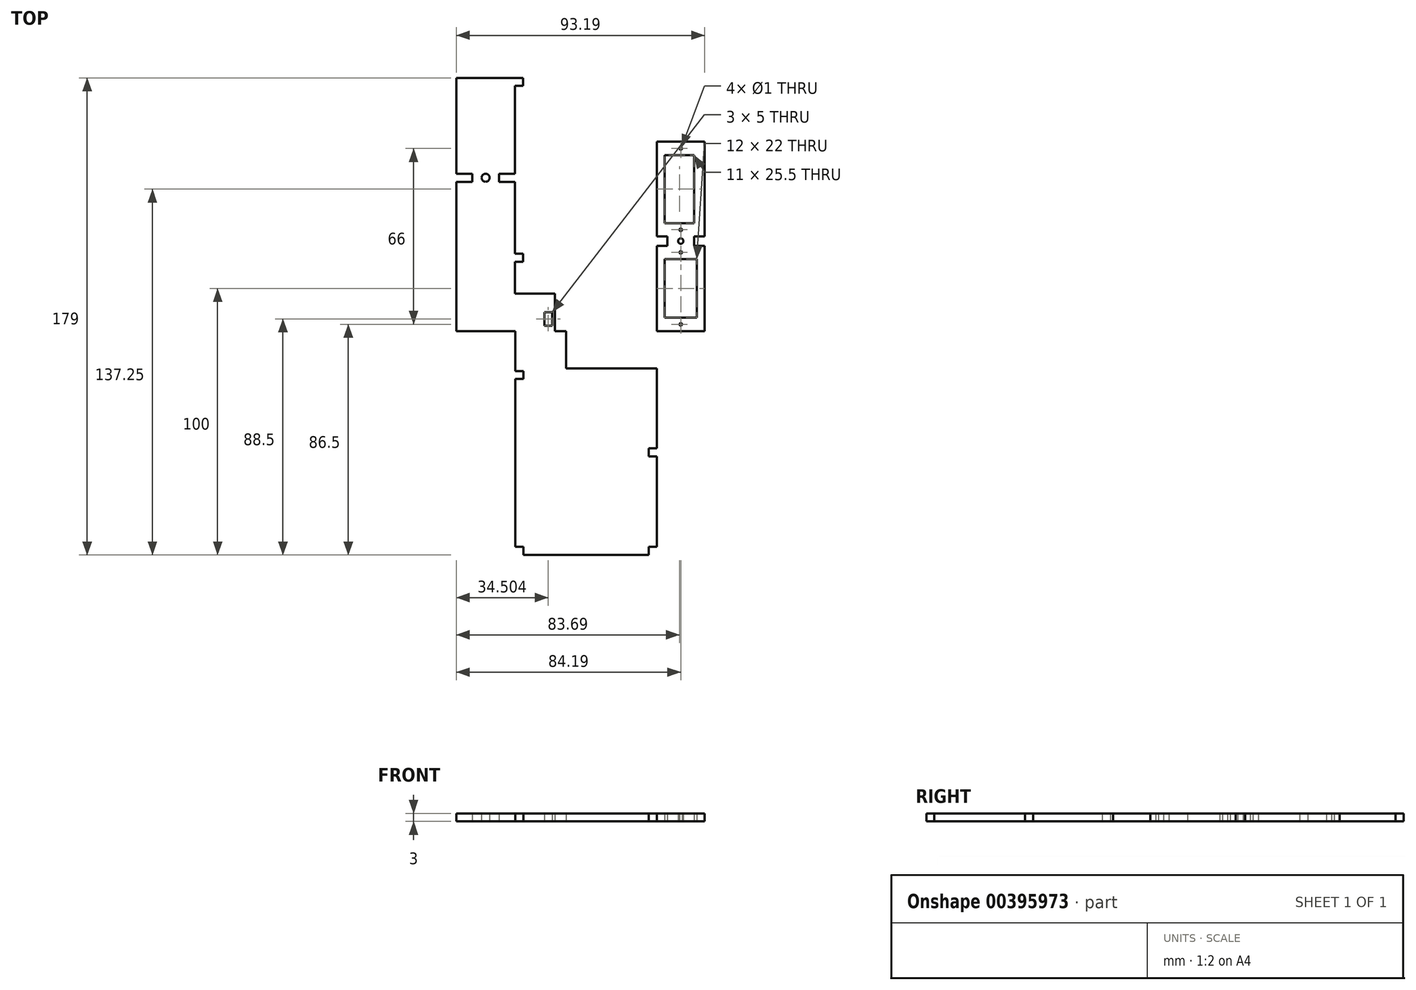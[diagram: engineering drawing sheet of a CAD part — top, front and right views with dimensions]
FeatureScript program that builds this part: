
annotation { "Feature Type Name" : "Feature", "Feature Type Description" : "" }
export const myFeature = defineFeature(function(context is Context, id is Id, definition is map)
    precondition{}
    {
        {
            var Q0;
            Q0=qCreatedBy(makeId("Top.planeOp"),FACE);
            var sketch = newSketch(context, id + "F0", { "sketchPlane" : qUnion([Q0])});
            skLineSegment(sketch, "E0", {"start": v(0, 0) * mm, "end": v(0, 32) * mm});
            skLineSegment(sketch, "E1", {"start": v(0, 71) * mm, "end": v(18, 71) * mm});
            skLineSegment(sketch, "E2", {"start": v(18, 71) * mm, "end": v(18, 35.5) * mm});
            skLineSegment(sketch, "E3", {"start": v(18, 0) * mm, "end": v(0, 0) * mm});
            skLineSegment(sketch, "E4", {"start": v(18, 71) * mm, "end": v(18, 38) * mm});
            skLineSegment(sketch, "E5", {"start": v(9, 5) * mm, "end": v(18, 5) * mm});
            skLineSegment(sketch, "E6", {"start": v(18, 5) * mm, "end": v(0, 5) * mm});
            skLineSegment(sketch, "E7", {"start": v(2.25, 5) * mm, "end": v(9, 5) * mm});
            skLineSegment(sketch, "E8", {"start": v(3, 5) * mm, "end": v(4.5, 5) * mm});
            skLineSegment(sketch, "E9", {"start": v(0, 5) * mm, "end": v(0, 32) * mm});
            skLineSegment(sketch, "E10", {"start": v(0, 5) * mm, "end": v(0, 27) * mm});
            skLineSegment(sketch, "E11", {"start": v(0, 27) * mm, "end": v(18, 27) * mm});
            skLineSegment(sketch, "E12", {"start": v(0, 5) * mm, "end": v(2.25, 5) * mm});
            skLineSegment(sketch, "E13", {"start": v(0, 5) * mm, "end": v(3, 5) * mm});
            skLineSegment(sketch, "E14", {"start": v(3, 5) * mm, "end": v(3, 27) * mm});
            skLineSegment(sketch, "E15", {"start": v(18, 5) * mm, "end": v(13.5, 5) * mm});
            skLineSegment(sketch, "E16", {"start": v(18, 5) * mm, "end": v(15, 5) * mm});
            skLineSegment(sketch, "E17", {"start": v(15, 5) * mm, "end": v(15, 27) * mm});
            skLineSegment(sketch, "E18", {"start": v(0, 27) * mm, "end": v(0, 32) * mm});
            skLineSegment(sketch, "E19", {"start": v(0, 32) * mm, "end": v(18, 32) * mm});
            skLineSegment(sketch, "E20", {"start": v(0, 32) * mm, "end": v(4, 32) * mm});
            skLineSegment(sketch, "E21", {"start": v(4, 32) * mm, "end": v(4, 35.5) * mm});
            skLineSegment(sketch, "E22", {"start": v(4, 35.5) * mm, "end": v(18, 35.5) * mm});
            skLineSegment(sketch, "E23", {"start": v(18, 32) * mm, "end": v(14, 32) * mm});
            skLineSegment(sketch, "E24", {"start": v(14, 32) * mm, "end": v(14, 35.5) * mm});
            skLineSegment(sketch, "E25", {"start": v(4, 35.5) * mm, "end": v(0, 35.5) * mm});
            skLineSegment(sketch, "E26", {"start": v(4, 35.5) * mm, "end": v(4, 40.5) * mm});
            skLineSegment(sketch, "E27", {"start": v(4, 40.5) * mm, "end": v(18, 40.5) * mm});
            skLineSegment(sketch, "E28", {"start": v(18, 40.5) * mm, "end": v(0, 40.5) * mm});
            skLineSegment(sketch, "E29", {"start": v(0, 40.5) * mm, "end": v(3, 40.5) * mm});
            skLineSegment(sketch, "E30", {"start": v(3, 40.5) * mm, "end": v(3, 71) * mm});
            skLineSegment(sketch, "E31", {"start": v(3, 71) * mm, "end": v(14, 71) * mm});
            skLineSegment(sketch, "E32", {"start": v(14, 71) * mm, "end": v(14, 40.5) * mm});
            skLineSegment(sketch, "E33", {"start": v(0, 32) * mm, "end": v(0, 0) * mm});
            skLineSegment(sketch, "E34", {"start": v(18, 0) * mm, "end": v(18, 27) * mm});
            skLineSegment(sketch, "E35", {"start": v(18, 27) * mm, "end": v(18, 32) * mm});
            skLineSegment(sketch, "E36", {"start": v(18, 71) * mm, "end": v(18, 40.5) * mm});
            skLineSegment(sketch, "E37", {"start": v(0, 71) * mm, "end": v(0, 66) * mm});
            skLineSegment(sketch, "E38", {"start": v(0, 66) * mm, "end": v(18, 66) * mm});
            skLineSegment(sketch, "E39", {"start": v(0, 66) * mm, "end": v(0, 40.5) * mm});
            skLineSegment(sketch, "E40", {"start": v(0, 35.5) * mm, "end": v(0, 71) * mm});
            skLineSegment(sketch, "E41.trimOffspring", {"start": v(18, 32) * mm, "end": v(18, 0) * mm});
            skPoint(sketch, "E42.end.orphan", {"position": v(3, 0) * mm});
            skLineSegment(sketch, "E43", {"start": v(3, 5) * mm, "end": v(2.25, 5) * mm});
            skLineSegment(sketch, "E44", {"start": v(0, 5) * mm, "end": v(18, 5) * mm});
            skLineSegment(sketch, "E45", {"start": v(4, 35.5) * mm, "end": v(4, 33.75) * mm});
            skLineSegment(sketch, "E46", {"start": v(4, 33.75) * mm, "end": v(14, 33.75) * mm});
            skLineSegment(sketch, "E47", {"start": v(14, 35.5) * mm, "end": v(9, 35.5) * mm});
            skLineSegment(sketch, "E48", {"start": v(9, 35.5) * mm, "end": v(9, 32) * mm});
            skCircle(sketch, "E49", {"center": v(9, 33.75) * mm, "radius": 1 * mm});
            skLineSegment(sketch, "E50", {"start": v(3, 71) * mm, "end": v(3, 68.5) * mm});
            skLineSegment(sketch, "E51", {"start": v(3, 68.5) * mm, "end": v(14, 68.5) * mm});
            skLineSegment(sketch, "E52", {"start": v(14, 68.5) * mm, "end": v(14, 71) * mm});
            skLineSegment(sketch, "E53", {"start": v(9, 71) * mm, "end": v(9, 66) * mm});
            skCircle(sketch, "E54", {"center": v(9, 68.5) * mm, "radius": 0.5 * mm});
            skLineSegment(sketch, "E55", {"start": v(0, 5) * mm, "end": v(8, 5) * mm});
            skLineSegment(sketch, "E56", {"start": v(0, 0) * mm, "end": v(0, 2.5) * mm});
            skLineSegment(sketch, "E57", {"start": v(0, 2.5) * mm, "end": v(18, 2.5) * mm});
            skLineSegment(sketch, "E58", {"start": v(0, 0) * mm, "end": v(9, 0) * mm});
            skLineSegment(sketch, "E59", {"start": v(9, 0) * mm, "end": v(9, 5) * mm});
            skCircle(sketch, "E60", {"center": v(9, 2.5) * mm, "radius": 0.5 * mm});
            skLineSegment(sketch, "E61", {"start": v(0, 29.5) * mm, "end": v(18, 29.5) * mm});
            skLineSegment(sketch, "E62", {"start": v(9, 27) * mm, "end": v(9, 32) * mm});
            skCircle(sketch, "E63", {"center": v(9, 29.5) * mm, "radius": 0.5 * mm});
            skLineSegment(sketch, "E64", {"start": v(9, 32) * mm, "end": v(9, 40.5) * mm});
            skLineSegment(sketch, "E65", {"start": v(0, 40.5) * mm, "end": v(0, 38) * mm});
            skLineSegment(sketch, "E66", {"start": v(0, 38) * mm, "end": v(18, 38) * mm});
            skCircle(sketch, "E67", {"center": v(9, 38) * mm, "radius": 0.5 * mm});
            skSolve(sketch);
        }
        {
            var Q0;
            Q0 = qSketchRegion(id + "F0", true);
            var Q1;
            {var subQ1=sQuery(id+"F0.wireOp",EDGE,"E26");var subQ5=sQuery(id+"F0.wireOp",EDGE,"E28");var subQ6=makeQuery(id+"F0.imprint","INTERSECT",VERTEX,{"derivedFrom":[subQ1,subQ5]});Q1=makeQuery(id+"F0.imprint","IMPRINT",FACE,{"disambiguationData":[TD([[makeQuery(id+"F0.imprint","IMPRINT",EDGE,{"disambiguationData":[TD([[subQ6,1.0]])],"derivedFrom":subQ1}),-1.0]])]});}
            var Q2;
            {var subQ0=sQuery(id+"F0.wireOp",EDGE,"E53");var subQ1=sQuery(id+"F0.wireOp",EDGE,"E38");var subQ2=makeQuery(id+"F0.imprint","INTERSECT",VERTEX,{"derivedFrom":[subQ1,subQ0]});Q2=makeQuery(id+"F0.imprint","IMPRINT",FACE,{"disambiguationData":[TD([[makeQuery(id+"F0.imprint","IMPRINT",EDGE,{"disambiguationData":[TD([[subQ2,1.0]])],"derivedFrom":subQ1}),1.0]])]});}
            var Q3;
            {var subQ0=sQuery(id+"F0.wireOp",EDGE,"E53");var subQ1=sQuery(id+"F0.wireOp",EDGE,"E38");var subQ2=makeQuery(id+"F0.imprint","INTERSECT",VERTEX,{"derivedFrom":[subQ1,subQ0]});Q3=makeQuery(id+"F0.imprint","IMPRINT",FACE,{"disambiguationData":[TD([[makeQuery(id+"F0.imprint","IMPRINT",EDGE,{"disambiguationData":[TD([[subQ2,-1.0]])],"derivedFrom":subQ1}),1.0]])]});}
            extrude(context, id + "F1", {"entities" : qUnion([Q0, Q1, Q2, Q3]), "depth" : 3 * mm});
        }
        {
            var Q0;
            Q0=qCreatedBy(makeId("Top.planeOp"),FACE);
            var sketch = newSketch(context, id + "F2", { "sketchPlane" : qUnion([Q0])});
            skLineSegment(sketch, "E68", {"start": v(-53, 0) * mm, "end": v(-53, -84) * mm});
            skLineSegment(sketch, "E69", {"start": v(-53, -84) * mm, "end": v(0, -84) * mm});
            skLineSegment(sketch, "E70", {"start": v(0, -84) * mm, "end": v(0, -14) * mm});
            skLineSegment(sketch, "E71", {"start": v(0, -14) * mm, "end": v(-34, -14) * mm});
            skLineSegment(sketch, "E72", {"start": v(-34, -14) * mm, "end": v(-34, 0) * mm});
            skLineSegment(sketch, "E73", {"start": v(-34, 0) * mm, "end": v(-53, 0) * mm});
            skLineSegment(sketch, "E74", {"start": v(-53, -84) * mm, "end": v(-53, -81) * mm});
            skLineSegment(sketch, "E75", {"start": v(-53, -81) * mm, "end": v(-50, -81) * mm});
            skLineSegment(sketch, "E76", {"start": v(-50, -81) * mm, "end": v(-50, -84) * mm});
            skLineSegment(sketch, "E77", {"start": v(0, -84) * mm, "end": v(0, -81) * mm});
            skLineSegment(sketch, "E78", {"start": v(0, -81) * mm, "end": v(-3, -81) * mm});
            skLineSegment(sketch, "E79", {"start": v(-3, -81) * mm, "end": v(-3, -84) * mm});
            skLineSegment(sketch, "E80", {"start": v(0, -14) * mm, "end": v(0, -44) * mm});
            skLineSegment(sketch, "E81", {"start": v(0, -44) * mm, "end": v(-3, -44) * mm});
            skLineSegment(sketch, "E82", {"start": v(-3, -44) * mm, "end": v(-3, -47) * mm});
            skLineSegment(sketch, "E83", {"start": v(-3, -47) * mm, "end": v(0, -47) * mm});
            skLineSegment(sketch, "E84", {"start": v(-53, 0) * mm, "end": v(-53, -15) * mm});
            skLineSegment(sketch, "E85", {"start": v(-53, -15) * mm, "end": v(-50, -15) * mm});
            skLineSegment(sketch, "E86", {"start": v(-50, -15) * mm, "end": v(-50, -18) * mm});
            skLineSegment(sketch, "E87", {"start": v(-50, -18) * mm, "end": v(-53, -18) * mm});
            skSolve(sketch);
        }
        {
            var Q0;
            Q0=makeQuery(id+"F2.imprint","IMPRINT",FACE,{"disambiguationData":[TD([[makeQuery(id+"F2.imprint","IMPRINT",EDGE,{"derivedFrom":sQuery(id+"F2.wireOp",EDGE,"E71")}),1.0]])]});
            extrude(context, id + "F3", {"entities" : qUnion([Q0]), "depth" : 3 * mm});
        }
        {
            var Q0;
            Q0=qCreatedBy(makeId("Top.planeOp"),FACE);
            var sketch = newSketch(context, id + "F4", { "sketchPlane" : qUnion([Q0])});
            skLineSegment(sketch, "E88", {"start": v(-75.19, 0) * mm, "end": v(-75.19, 56) * mm});
            skLineSegment(sketch, "E89", {"start": v(-75.19, 95) * mm, "end": v(-50.19, 95) * mm});
            skLineSegment(sketch, "E90", {"start": v(-50.19, 95) * mm, "end": v(-50.19, 92) * mm});
            skLineSegment(sketch, "E91", {"start": v(-50.19, 92) * mm, "end": v(-53.19, 92) * mm});
            skLineSegment(sketch, "E92", {"start": v(-53.19, 92) * mm, "end": v(-53.19, 59) * mm});
            skLineSegment(sketch, "E93", {"start": v(-53.19, 59) * mm, "end": v(-59.19, 59) * mm});
            skLineSegment(sketch, "E94", {"start": v(-59.19, 59) * mm, "end": v(-59.19, 56) * mm});
            skLineSegment(sketch, "E95", {"start": v(-59.19, 56) * mm, "end": v(-53.19, 56) * mm});
            skLineSegment(sketch, "E96", {"start": v(-53.19, 56) * mm, "end": v(-53.19, 29) * mm});
            skLineSegment(sketch, "E97", {"start": v(-53.19, 29) * mm, "end": v(-50.19, 29) * mm});
            skLineSegment(sketch, "E98", {"start": v(-50.19, 29) * mm, "end": v(-50.19, 26) * mm});
            skLineSegment(sketch, "E99", {"start": v(-50.19, 14) * mm, "end": v(-38.19, 14) * mm});
            skLineSegment(sketch, "E100", {"start": v(-38.19, 14) * mm, "end": v(-38.19, 0) * mm});
            skLineSegment(sketch, "E101", {"start": v(-38.19, 0) * mm, "end": v(-75.19, 0) * mm});
            skPoint(sketch, "E102.endSnap0", {"position": v(-38.19, 7) * mm});
            skLineSegment(sketch, "E103", {"start": v(-39.19, 2) * mm, "end": v(-42.19, 2) * mm});
            skLineSegment(sketch, "E104", {"start": v(-42.19, 2) * mm, "end": v(-42.19, 7) * mm});
            skLineSegment(sketch, "E105", {"start": v(-42.19, 7) * mm, "end": v(-39.19, 7) * mm});
            skLineSegment(sketch, "E106", {"start": v(-39.19, 7) * mm, "end": v(-39.19, 2) * mm});
            skPoint(sketch, "E102.end.orphan", {"position": v(-42.19, 7) * mm});
            skPoint(sketch, "E102.start.orphan", {"position": v(-42.19, 14) * mm});
            skPoint(sketch, "E107.end.orphan", {"position": v(-39.19, 3.73) * mm});
            skPoint(sketch, "E108.start.orphan", {"position": v(-39.19, 0) * mm});
            skLineSegment(sketch, "E109", {"start": v(-75.19, 56) * mm, "end": v(-69.19, 56) * mm});
            skLineSegment(sketch, "E110", {"start": v(-69.19, 56) * mm, "end": v(-69.19, 59) * mm});
            skLineSegment(sketch, "E111", {"start": v(-69.19, 59) * mm, "end": v(-75.19, 59) * mm});
            skLineSegment(sketch, "E112", {"start": v(-69.19, 59) * mm, "end": v(-59.19, 59) * mm});
            skLineSegment(sketch, "E113", {"start": v(-69.19, 56) * mm, "end": v(-59.19, 56) * mm});
            skLineSegment(sketch, "E114", {"start": v(-64.19, 59) * mm, "end": v(-64.19, 56) * mm});
            skLineSegment(sketch, "E115", {"start": v(-69.19, 57.5) * mm, "end": v(-59.19, 57.5) * mm});
            skCircle(sketch, "E116", {"center": v(-64.19, 57.5) * mm, "radius": 1.5 * mm});
            skLineSegment(sketch, "E117", {"start": v(-50.19, 26) * mm, "end": v(-53.19, 26) * mm});
            skLineSegment(sketch, "E118", {"start": v(-53.19, 26) * mm, "end": v(-53.19, 14) * mm});
            skLineSegment(sketch, "E119", {"start": v(-53.19, 14) * mm, "end": v(-50.19, 14) * mm});
            skLineSegment(sketch, "E120.trimOffspring", {"start": v(-75.19, 59) * mm, "end": v(-75.19, 95) * mm});
            skSolve(sketch);
        }
        {
            var Q0;
            Q0 = qSketchRegion(id + "F4", true);
            extrude(context, id + "F5", {"entities" : qUnion([Q0]), "operationType" : NewBodyOperationType.ADD, "depth" : 3 * mm});
        }
    });
